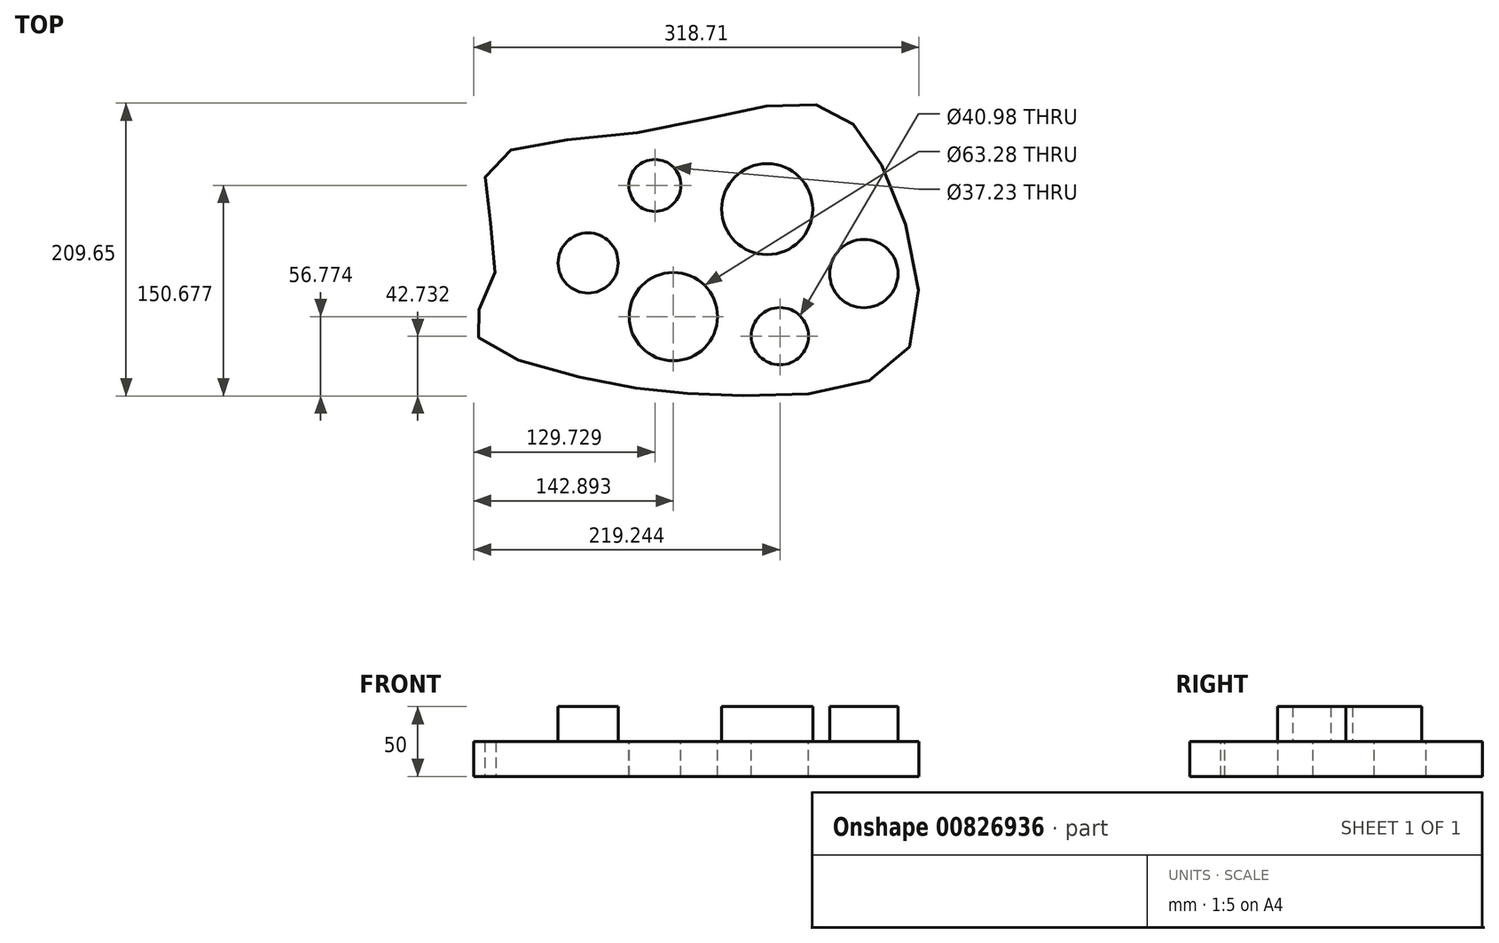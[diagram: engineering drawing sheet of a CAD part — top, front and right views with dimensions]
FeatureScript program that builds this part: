
annotation { "Feature Type Name" : "Feature", "Feature Type Description" : "" }
export const myFeature = defineFeature(function(context is Context, id is Id, definition is map)
    precondition{}
    {
        {
            var Q0;
            Q0=qCreatedBy(makeId("Top.planeOp"),FACE);
            var sketch = newSketch(context, id + "F0", { "sketchPlane" : qUnion([Q0])});
            skFitSpline(sketch, "E0", {"points": [v(-166.43, 28.05) * mm, v(-171.33, 103.25) * mm, v(-63.13, 128.22) * mm, v(62.67, 148.16) * mm, v(114.11, 96.79) * mm, v(126.87, -30.62) * mm, v(8.73, -60.32) * mm, v(-93.75, -49.57) * mm, v(-181.2, -13.92) * mm, v(-166.43, 28.05) * mm]});
            skSolve(sketch);
        }
        {
            var Q0;
            Q0=makeQuery(id+"F0.imprint","IMPRINT",FACE,{"disambiguationData":[TD([[makeQuery(id+"F0.imprint","IMPRINT",EDGE,{"derivedFrom":sQuery(id+"F0.wireOp",EDGE,"E0")}),-1.0]])]});
            extrude(context, id + "F1", {"entities" : qUnion([Q0]), "depth" : 25 * mm, "offsetDistance" : 25 * mm});
        }
        {
            var Q0;
            Q0=makeQuery(id+"F1.opExtrude","CAP_FACE",FACE,{"disambiguationData":[OSD([sQuery(id+"F0.wireOp",EDGE,"E0")])],"isStart":false});
            var sketch = newSketch(context, id + "F2", { "sketchPlane" : qUnion([Q0])});
            skCircle(sketch, "E1", {"center": v(-99.85, 34.73) * mm, "radius": 21.51 * mm});
            skCircle(sketch, "E2", {"center": v(28.37, 73.29) * mm, "radius": 32.58 * mm});
            skCircle(sketch, "E3", {"center": v(97.59, 27.12) * mm, "radius": 24.45 * mm});
            skSolve(sketch);
        }
        {
            var Q0;
            Q0=makeQuery(id+"F2.imprint","IMPRINT",FACE,{"disambiguationData":[TD([[makeQuery(id+"F2.imprint","IMPRINT",EDGE,{"derivedFrom":sQuery(id+"F2.wireOp",EDGE,"E1")}),1.0]])]});
            var Q1;
            Q1=makeQuery(id+"F2.imprint","IMPRINT",FACE,{"disambiguationData":[TD([[makeQuery(id+"F2.imprint","IMPRINT",EDGE,{"derivedFrom":sQuery(id+"F2.wireOp",EDGE,"E2")}),1.0]])]});
            var Q2;
            Q2=makeQuery(id+"F2.imprint","IMPRINT",FACE,{"disambiguationData":[TD([[makeQuery(id+"F2.imprint","IMPRINT",EDGE,{"derivedFrom":sQuery(id+"F2.wireOp",EDGE,"E3")}),1.0]])]});
            extrude(context, id + "F3", {"entities" : qUnion([Q0, Q1, Q2]), "operationType" : NewBodyOperationType.ADD, "depth" : 25 * mm, "offsetDistance" : 25 * mm});
        }
        {
            var Q0;
            Q0=makeQuery(id+"F1.opExtrude","CAP_FACE",FACE,{"disambiguationData":[OSD([sQuery(id+"F0.wireOp",EDGE,"E0")])],"isStart":false});
            var sketch = newSketch(context, id + "F4", { "sketchPlane" : qUnion([Q0])});
            skCircle(sketch, "E4", {"center": v(-52.03, 90.24) * mm, "radius": 18.62 * mm});
            skCircle(sketch, "E5", {"center": v(-38.87, -3.67) * mm, "radius": 31.64 * mm});
            skCircle(sketch, "E6", {"center": v(37.48, -17.7) * mm, "radius": 20.49 * mm});
            skSolve(sketch);
        }
        {
            var Q0;
            Q0=makeQuery(id+"F4.imprint","IMPRINT",FACE,{"disambiguationData":[TD([[makeQuery(id+"F4.imprint","IMPRINT",EDGE,{"derivedFrom":sQuery(id+"F4.wireOp",EDGE,"E4")}),1.0]])]});
            var Q1;
            Q1=makeQuery(id+"F4.imprint","IMPRINT",FACE,{"disambiguationData":[TD([[makeQuery(id+"F4.imprint","IMPRINT",EDGE,{"derivedFrom":sQuery(id+"F4.wireOp",EDGE,"E5")}),1.0]])]});
            var Q2;
            Q2=makeQuery(id+"F4.imprint","IMPRINT",FACE,{"disambiguationData":[TD([[makeQuery(id+"F4.imprint","IMPRINT",EDGE,{"derivedFrom":sQuery(id+"F4.wireOp",EDGE,"E6")}),1.0]])]});
            extrude(context, id + "F5", {"entities" : qUnion([Q0, Q1, Q2]), "operationType" : NewBodyOperationType.REMOVE, "oppositeDirection" : true, "depth" : 25 * mm, "offsetDistance" : 25 * mm});
        }
    });
